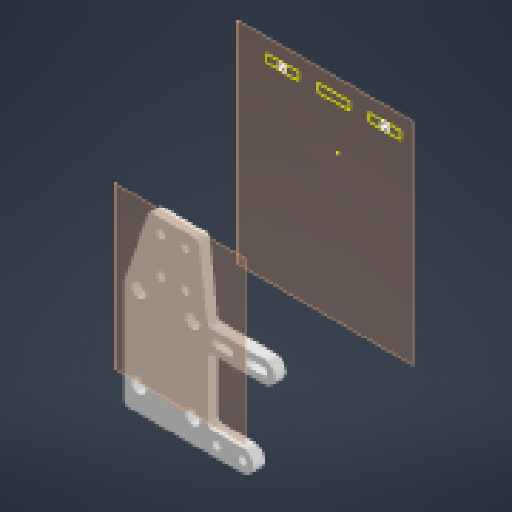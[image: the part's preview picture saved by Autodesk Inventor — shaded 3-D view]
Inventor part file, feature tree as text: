
AUTODESK INVENTOR PART (.ipt)
format: ipt  version: 2025 (Build 290162000, 162)  size: 359,936 bytes
history: native  units: mm
features: reference x12, sketch x5, extrude x4, other x4, plane x2, fillet x1
ambient origin geometry x8: Origin, YZ Plane, XZ Plane, XY Plane, X Axis, Y Axis, Z Axis, Center Point
bodies: Solid1 (feature_tree)
feature tree (28):
  plane  "Work Plane1"
  sketch  "Sketch1"  dims[d3=4.5mm d4=0.0mm d5=3.2mm]
  plane  "Work Plane2"
  sketch  "Sketch2"  dims[d6=3.2mm d7=3.2mm]
  extrude  "Extrusion1"  Depth=4.5mm
  extrude  "Extrusion2"  Depth=3.2mm
  extrude  "Extrusion3"  Depth=10.58mm
  fillet  "Fillet1"  Radius=5.29mm
  extrude  "Extrusion4"  Depth=3.2mm
  reference  "Reference5"
  reference  "Reference6"
  reference  "Reference7"
  reference  "Reference8"
  reference  "Reference9"
  reference  "Reference10"
  reference  "Reference11"
  reference  "Reference12"
  reference  "Reference13"
  reference  "Reference14"
  reference  "Reference15"
  reference  "Reference16"
  sketch  "Sketch3"  dims[d8=3.2mm d9=10.58mm d10=5.29mm]
  sketch  "Sketch4"  dims[d11=10.58mm d12=3.2mm]
  sketch  "Sketch5"  dims[d13=3.2mm d14=3.0mm d15=3.0mm d16=4.5mm d17=0.0mm d22=3.5mm d23=0.0mm d24=2.0mm d25=6.0mm d26=6.0mm d27=6.0mm d28=6.0mm d29=3.5mm d30=0.0mm d43=6.0mm d44=8.0mm d45=20.0mm d46=6.0mm d47=3.0mm d48=6.0mm d49=3.0mm d50=3.0mm d51=3.0mm d52=4.4mm d56=8.0mm d58=10.0mm d59=17.35mm d60=6.27mm d61=6.27mm d62=15.0mm d63=3.2mm d64=3.2mm d65=3.2mm d66=3.2mm d67=6.0mm d68=6.0mm d69=6.0mm d70=6.0mm]
  other  "<userpath> 7 was better\Downloads\Hotend assembly\Hotend assembly.iam"
  other  "Hotend assembly.iam"
  other  "makerbot main plate v5:1"
  other  "Part119"
